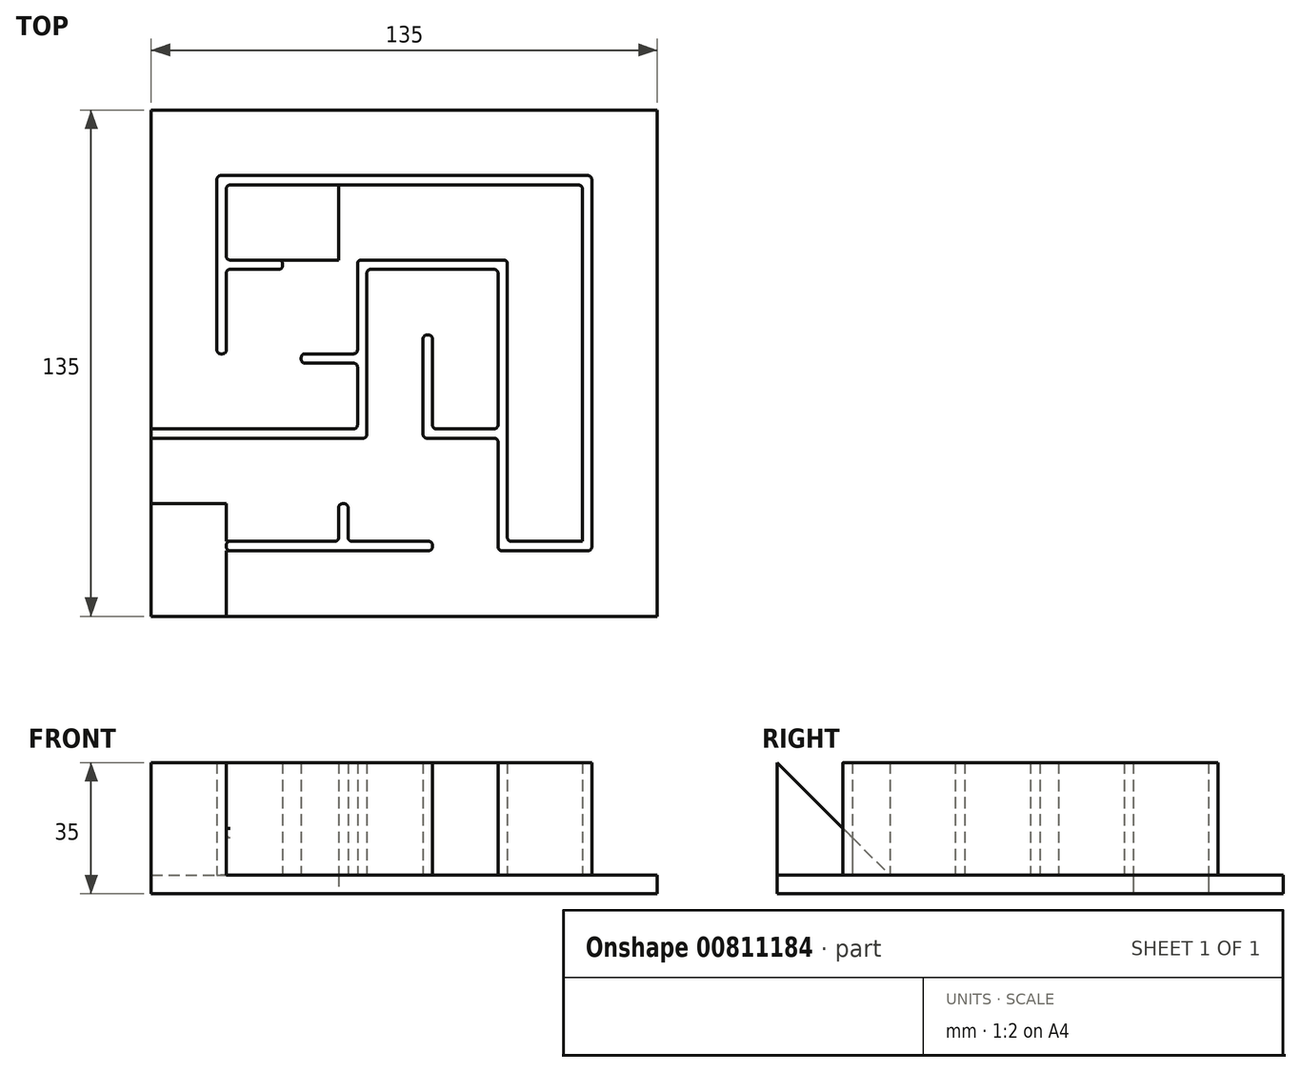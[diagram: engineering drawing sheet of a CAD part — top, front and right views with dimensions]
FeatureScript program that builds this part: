
annotation { "Feature Type Name" : "Feature", "Feature Type Description" : "" }
export const myFeature = defineFeature(function(context is Context, id is Id, definition is map)
    precondition{}
    {
        {
            var Q0;
            Q0=qCreatedBy(makeId("Top.planeOp"),FACE);
            var sketch = newSketch(context, id + "F0", { "sketchPlane" : qUnion([Q0])});
            skLineSegment(sketch, "E0.bottom", {"start": v(-67.5, 67.5) * mm, "end": v(67.5, 67.5) * mm});
            skLineSegment(sketch, "E0.top", {"start": v(-67.5, -67.5) * mm, "end": v(67.5, -67.5) * mm});
            skLineSegment(sketch, "E0.left", {"start": v(-67.5, 67.5) * mm, "end": v(-67.5, -67.5) * mm});
            skLineSegment(sketch, "E0.right", {"start": v(67.5, 67.5) * mm, "end": v(67.5, -67.5) * mm});
            skPoint(sketch, "E0.middle", {"position": v(0, 0) * mm});
            skLineSegment(sketch, "E1.bottom", {"start": v(-67.5, -67.5) * mm, "end": v(-47.5, -67.5) * mm});
            skLineSegment(sketch, "E1.top", {"start": v(-67.5, -37.5) * mm, "end": v(-47.5, -37.5) * mm});
            skLineSegment(sketch, "E1.left", {"start": v(-67.5, -67.5) * mm, "end": v(-67.5, -37.5) * mm});
            skLineSegment(sketch, "E1.right", {"start": v(-47.5, -67.5) * mm, "end": v(-47.5, -37.5) * mm});
            skLineSegment(sketch, "E2", {"start": v(-67.5, -17.5) * mm, "end": v(-12.5, -17.5) * mm});
            skLineSegment(sketch, "E3", {"start": v(-12.5, -17.5) * mm, "end": v(-12.5, 27.5) * mm});
            skLineSegment(sketch, "E4", {"start": v(-12.5, 27.5) * mm, "end": v(27.5, 27.5) * mm});
            skLineSegment(sketch, "E5", {"start": v(27.5, 27.5) * mm, "end": v(27.5, -47.5) * mm});
            skLineSegment(sketch, "E6", {"start": v(27.5, -47.5) * mm, "end": v(47.5, -47.5) * mm});
            skLineSegment(sketch, "E7", {"start": v(47.5, -47.5) * mm, "end": v(47.5, 47.5) * mm});
            skLineSegment(sketch, "E8", {"start": v(47.5, 47.5) * mm, "end": v(-47.5, 47.5) * mm});
            skLineSegment(sketch, "E9", {"start": v(-47.5, 47.5) * mm, "end": v(-47.5, 2.5) * mm});
            skLineSegment(sketch, "E10", {"start": v(27.5, -17.5) * mm, "end": v(7.5, -17.5) * mm});
            skLineSegment(sketch, "E11", {"start": v(7.5, -17.5) * mm, "end": v(7.5, 7.5) * mm});
            skLineSegment(sketch, "E12", {"start": v(-47.5, -47.5) * mm, "end": v(7.5, -47.5) * mm});
            skLineSegment(sketch, "E13", {"start": v(-12.5, 2.5) * mm, "end": v(-27.5, 2.5) * mm});
            skLineSegment(sketch, "E14", {"start": v(-47.5, 27.5) * mm, "end": v(-32.5, 27.5) * mm});
            skLineSegment(sketch, "E15", {"start": v(-17.5, -47.5) * mm, "end": v(-17.5, -37.5) * mm});
            skLineSegment(sketch, "E16.0", {"start": v(-10, -20) * mm, "end": v(-10, 27.5) * mm});
            skLineSegment(sketch, "E16.1", {"start": v(-67.5, -20) * mm, "end": v(-10, -20) * mm});
            skLineSegment(sketch, "E17.0", {"start": v(-47.5, -50) * mm, "end": v(7.5, -50) * mm});
            skLineSegment(sketch, "E18.0", {"start": v(-50, 50) * mm, "end": v(-50, 2.5) * mm});
            skLineSegment(sketch, "E18.1", {"start": v(50, 50) * mm, "end": v(-50, 50) * mm});
            skLineSegment(sketch, "E18.2", {"start": v(-12.5, 25) * mm, "end": v(25, 25) * mm});
            skLineSegment(sketch, "E18.3", {"start": v(25, 25) * mm, "end": v(25, -50) * mm});
            skLineSegment(sketch, "E18.4", {"start": v(25, -50) * mm, "end": v(50, -50) * mm});
            skLineSegment(sketch, "E18.5", {"start": v(50, -50) * mm, "end": v(50, 50) * mm});
            skLineSegment(sketch, "E19.0", {"start": v(-47.5, 25) * mm, "end": v(-32.5, 25) * mm});
            skLineSegment(sketch, "E20.0", {"start": v(-12.5, 0) * mm, "end": v(-27.5, 0) * mm});
            skLineSegment(sketch, "E21.0", {"start": v(5, -20) * mm, "end": v(5, 7.5) * mm});
            skLineSegment(sketch, "E21.1", {"start": v(27.5, -20) * mm, "end": v(5, -20) * mm});
            skLineSegment(sketch, "E22", {"start": v(7.5, -47.5) * mm, "end": v(7.5, -50) * mm});
            skLineSegment(sketch, "E23", {"start": v(-50, 2.5) * mm, "end": v(-47.5, 2.5) * mm});
            skLineSegment(sketch, "E24", {"start": v(5, 7.5) * mm, "end": v(7.5, 7.5) * mm});
            skLineSegment(sketch, "E25", {"start": v(-27.5, 0) * mm, "end": v(-27.5, 2.5) * mm});
            skLineSegment(sketch, "E26", {"start": v(-32.5, 25) * mm, "end": v(-32.5, 27.5) * mm});
            skLineSegment(sketch, "E27", {"start": v(-17.5, -37.5) * mm, "end": v(-15, -37.5) * mm});
            skLineSegment(sketch, "E28", {"start": v(-15, -37.5) * mm, "end": v(-15, -47.5) * mm});
            skLineSegment(sketch, "E29.bottom", {"start": v(-47.5, 27.5) * mm, "end": v(-17.5, 27.5) * mm});
            skLineSegment(sketch, "E29.top", {"start": v(-47.5, 47.5) * mm, "end": v(-17.5, 47.5) * mm});
            skLineSegment(sketch, "E29.left", {"start": v(-47.5, 27.5) * mm, "end": v(-47.5, 47.5) * mm});
            skLineSegment(sketch, "E29.right", {"start": v(-17.5, 27.5) * mm, "end": v(-17.5, 47.5) * mm});
            skSolve(sketch);
        }
        {
            var Q0;
            {var subQ29=sQuery(id+"F0.wireOp",EDGE,"E0.bottom");Q0=makeQuery(id+"F0.imprint","IMPRINT",FACE,{"disambiguationData":[TD([[makeQuery(id+"F0.imprint","IMPRINT",EDGE,{"derivedFrom":subQ29}),-1.0]])]});}
            extrude(context, id + "F1", {"entities" : qUnion([Q0]), "depth" : 5 * mm, "offsetDistance" : 25 * mm});
        }
        {
            var Q0;
            {var subQ0=sQuery(id+"F0.wireOp",EDGE,"E1.top");Q0=makeQuery(id+"F0.imprint","IMPRINT",FACE,{"disambiguationData":[TD([[makeQuery(id+"F0.imprint","IMPRINT",EDGE,{"derivedFrom":subQ0}),-1.0]])]});}
            extrude(context, id + "F2", {"entities" : qUnion([Q0]), "operationType" : NewBodyOperationType.ADD, "depth" : 35 * mm, "offsetDistance" : 25 * mm});
        }
        {
            var Q0;
            Q0=makeQuery(id+"F2.opExtrude","SWEPT_FACE",FACE,{"disambiguationData":[OSD([sQuery(id+"F0.wireOp",EDGE,"E1.right")])]});
            var sketch = newSketch(context, id + "F3", { "sketchPlane" : qUnion([Q0])});
            skLineSegment(sketch, "E30", {"start": v(-67.5, 35) * mm, "end": v(-37.5, 5) * mm});
            skSolve(sketch);
        }
        {
            var Q0;
            Q0=makeQuery(id+"F3.imprint","IMPRINT",FACE,{"disambiguationData":[TD([[makeQuery(id+"F3.imprint","IMPRINT",EDGE,{"derivedFrom":sQuery(id+"F3.wireOp",EDGE,"E30")}),1.0]])]});
            extrude(context, id + "F4", {"entities" : qUnion([Q0]), "operationType" : NewBodyOperationType.REMOVE, "oppositeDirection" : true, "depth" : 25 * mm, "offsetDistance" : 25 * mm});
        }
        {
            var Q0;
            {var subQ3=sQuery(id+"F0.wireOp",EDGE,"E6");Q0=makeQuery(id+"F0.imprint","IMPRINT",FACE,{"disambiguationData":[TD([[makeQuery(id+"F0.imprint","IMPRINT",EDGE,{"derivedFrom":subQ3}),-1.0]])]});}
            var Q1;
            {var subQ6=sQuery(id+"F0.wireOp",EDGE,"E17.0");Q1=makeQuery(id+"F0.imprint","IMPRINT",FACE,{"disambiguationData":[TD([[makeQuery(id+"F0.imprint","IMPRINT",EDGE,{"derivedFrom":subQ6}),1.0]])]});}
            var Q2;
            {var subQ1=sQuery(id+"F0.wireOp",EDGE,"E2");Q2=makeQuery(id+"F0.imprint","IMPRINT",FACE,{"disambiguationData":[TD([[makeQuery(id+"F0.imprint","IMPRINT",EDGE,{"derivedFrom":subQ1}),-1.0]])]});}
            var Q3;
            {var subQ0=sQuery(id+"F0.wireOp",EDGE,"E13");Q3=makeQuery(id+"F0.imprint","IMPRINT",FACE,{"disambiguationData":[TD([[makeQuery(id+"F0.imprint","IMPRINT",EDGE,{"derivedFrom":subQ0}),1.0]])]});}
            var Q4;
            {var subQ0=sQuery(id+"F0.wireOp",EDGE,"E14");Q4=makeQuery(id+"F0.imprint","IMPRINT",FACE,{"disambiguationData":[TD([[makeQuery(id+"F0.imprint","IMPRINT",EDGE,{"derivedFrom":subQ0}),-1.0]])]});}
            var Q5;
            {var subQ5=sQuery(id+"F0.wireOp",EDGE,"E4");var subQ7=sQuery(id+"F0.wireOp",EDGE,"E16.0");var subQ8=makeQuery(id+"F0.imprint","INTERSECT",VERTEX,{"derivedFrom":[subQ5,subQ7]});Q5=makeQuery(id+"F0.imprint","IMPRINT",FACE,{"disambiguationData":[TD([[makeQuery(id+"F0.imprint","IMPRINT",EDGE,{"disambiguationData":[TD([[subQ8,-1.0]])],"derivedFrom":subQ5}),-1.0]])]});}
            var Q6;
            {var subQ0=sQuery(id+"F0.wireOp",EDGE,"E4");var subQ1=sQuery(id+"F0.wireOp",EDGE,"E3");var subQ2=makeQuery(id+"F0.imprint","INTERSECT",VERTEX,{"derivedFrom":[subQ1,subQ0]});Q6=makeQuery(id+"F0.imprint","IMPRINT",FACE,{"disambiguationData":[TD([[makeQuery(id+"F0.imprint","IMPRINT",EDGE,{"disambiguationData":[TD([[subQ2,1.0]])],"derivedFrom":subQ1}),-1.0]])]});}
            var Q7;
            {var subQ1=sQuery(id+"F0.wireOp",EDGE,"E11");Q7=makeQuery(id+"F0.imprint","IMPRINT",FACE,{"disambiguationData":[TD([[makeQuery(id+"F0.imprint","IMPRINT",EDGE,{"derivedFrom":subQ1}),1.0]])]});}
            var Q8;
            {var subQ0=sQuery(id+"F0.wireOp",EDGE,"E21.1");var subQ1=sQuery(id+"F0.wireOp",EDGE,"E5");var subQ2=makeQuery(id+"F0.imprint","INTERSECT",VERTEX,{"derivedFrom":[subQ1,subQ0]});Q8=makeQuery(id+"F0.imprint","IMPRINT",FACE,{"disambiguationData":[TD([[makeQuery(id+"F0.imprint","IMPRINT",EDGE,{"disambiguationData":[TD([[subQ2,1.0]])],"derivedFrom":subQ1}),-1.0]])]});}
            var Q9;
            {var subQ2=sQuery(id+"F0.wireOp",EDGE,"E15");Q9=makeQuery(id+"F0.imprint","IMPRINT",FACE,{"disambiguationData":[TD([[makeQuery(id+"F0.imprint","IMPRINT",EDGE,{"derivedFrom":subQ2}),-1.0]])]});}
            var Q10;
            {var subQ2=sQuery(id+"F0.wireOp",EDGE,"E14");Q10=makeQuery(id+"F0.imprint","IMPRINT",FACE,{"disambiguationData":[TD([[makeQuery(id+"F0.imprint","IMPRINT",EDGE,{"derivedFrom":subQ2}),-1.0]])]});}
            extrude(context, id + "F5", {"entities" : qUnion([Q0, Q1, Q2, Q3, Q4, Q5, Q6, Q7, Q8, Q9, Q10]), "operationType" : NewBodyOperationType.ADD, "depth" : 35 * mm, "offsetDistance" : 25 * mm});
        }
        {
            var Q0;
            Q0=makeQuery(id+"F5.opExtrude","SWEPT_EDGE",EDGE,{"disambiguationData":[OSD([sQuery(id+"F0.wireOp",EDGE,"E17.0"),sQuery(id+"F0.wireOp",EDGE,"E22")])]});
            var Q1;
            Q1=makeQuery(id+"F5.opExtrude","SWEPT_EDGE",EDGE,{"disambiguationData":[OSD([sQuery(id+"F0.wireOp",EDGE,"E12"),sQuery(id+"F0.wireOp",EDGE,"E22")])]});
            var Q2;
            Q2=makeQuery(id+"F5.opExtrude","SWEPT_EDGE",EDGE,{"disambiguationData":[OSD([sQuery(id+"F0.wireOp",EDGE,"E16.0"),sQuery(id+"F0.wireOp",EDGE,"E16.1")])]});
            var Q3;
            Q3=makeQuery(id+"F5.opExtrude","SWEPT_EDGE",EDGE,{"disambiguationData":[OSD([sQuery(id+"F0.wireOp",EDGE,"E27"),sQuery(id+"F0.wireOp",EDGE,"E28")])]});
            var Q4;
            Q4=makeQuery(id+"F5.opExtrude","SWEPT_EDGE",EDGE,{"disambiguationData":[OSD([sQuery(id+"F0.wireOp",EDGE,"E21.0"),sQuery(id+"F0.wireOp",EDGE,"E21.1")])]});
            var Q5;
            Q5=makeQuery(id+"F5.opExtrude","SWEPT_EDGE",EDGE,{"disambiguationData":[OSD([sQuery(id+"F0.wireOp",EDGE,"E18.3"),sQuery(id+"F0.wireOp",EDGE,"E18.4")])]});
            var Q6;
            Q6=makeQuery(id+"F5.opExtrude","SWEPT_EDGE",EDGE,{"disambiguationData":[OSD([sQuery(id+"F0.wireOp",EDGE,"E18.4"),sQuery(id+"F0.wireOp",EDGE,"E18.5")])]});
            var Q7;
            Q7=makeQuery(id+"F5.opExtrude","SWEPT_EDGE",EDGE,{"disambiguationData":[OSD([sQuery(id+"F0.wireOp",EDGE,"E4"),sQuery(id+"F0.wireOp",EDGE,"E5")])]});
            var Q8;
            Q8=makeQuery(id+"F5.opExtrude","SWEPT_EDGE",EDGE,{"disambiguationData":[OSD([sQuery(id+"F0.wireOp",EDGE,"E18.1"),sQuery(id+"F0.wireOp",EDGE,"E18.5")])]});
            var Q9;
            Q9=makeQuery(id+"F5.opExtrude","SWEPT_EDGE",EDGE,{"disambiguationData":[OSD([sQuery(id+"F0.wireOp",EDGE,"E8"),sQuery(id+"F0.wireOp",EDGE,"E9")])]});
            var Q10;
            Q10=makeQuery(id+"F5.opExtrude","SWEPT_EDGE",EDGE,{"disambiguationData":[OSD([sQuery(id+"F0.wireOp",EDGE,"E20.0"),sQuery(id+"F0.wireOp",EDGE,"E25")])]});
            var Q11;
            {var subQ0=sQuery(id+"F0.wireOp",EDGE,"E1.right");var subQ1=sQuery(id+"F0.wireOp",EDGE,"E17.0");Q11=makeQuery(id+"F5.boolean.opBoolean","SPLIT",EDGE,{"disambiguationData":[topologyDisambiguationEdgeConnected([makeQuery(id+"F5.opExtrude","SWEPT_FACE",FACE,{"disambiguationData":[OSD([subQ0])]})])],"derivedFrom":makeQuery(id+"F5.opExtrude","SWEPT_EDGE",EDGE,{"disambiguationData":[OSD([subQ0,subQ1])]})});}
            var Q12;
            Q12=makeQuery(id+"F5.opExtrude","SWEPT_EDGE",EDGE,{"disambiguationData":[OSD([sQuery(id+"F0.wireOp",EDGE,"E9"),sQuery(id+"F0.wireOp",EDGE,"E19.0")])]});
            var Q13;
            Q13=makeQuery(id+"F5.opExtrude","SWEPT_EDGE",EDGE,{"disambiguationData":[OSD([sQuery(id+"F0.wireOp",EDGE,"E19.0"),sQuery(id+"F0.wireOp",EDGE,"E26")])]});
            var Q14;
            Q14=makeQuery(id+"F5.opExtrude","SWEPT_EDGE",EDGE,{"disambiguationData":[OSD([sQuery(id+"F0.wireOp",EDGE,"E14"),sQuery(id+"F0.wireOp",EDGE,"E26"),sQuery(id+"F0.wireOp",EDGE,"E29.bottom")])]});
            var Q15;
            Q15=makeQuery(id+"F5.opExtrude","SWEPT_EDGE",EDGE,{"disambiguationData":[OSD([sQuery(id+"F0.wireOp",EDGE,"E16.0"),sQuery(id+"F0.wireOp",EDGE,"E18.2")])]});
            var Q16;
            Q16=makeQuery(id+"F5.opExtrude","SWEPT_EDGE",EDGE,{"disambiguationData":[OSD([sQuery(id+"F0.wireOp",EDGE,"E11"),sQuery(id+"F0.wireOp",EDGE,"E24")])]});
            var Q17;
            Q17=makeQuery(id+"F5.opExtrude","SWEPT_EDGE",EDGE,{"disambiguationData":[OSD([sQuery(id+"F0.wireOp",EDGE,"E9"),sQuery(id+"F0.wireOp",EDGE,"E23")])]});
            var Q18;
            Q18=makeQuery(id+"F5.opExtrude","SWEPT_EDGE",EDGE,{"disambiguationData":[OSD([sQuery(id+"F0.wireOp",EDGE,"E18.0"),sQuery(id+"F0.wireOp",EDGE,"E23")])]});
            var Q19;
            {var subQ0=sQuery(id+"F0.wireOp",EDGE,"E1.right");var subQ1=sQuery(id+"F0.wireOp",EDGE,"E12");Q19=makeQuery(id+"F5.boolean.opBoolean","SPLIT",EDGE,{"disambiguationData":[topologyDisambiguationEdgeConnected([makeQuery(id+"F5.opExtrude","SWEPT_FACE",FACE,{"disambiguationData":[OSD([subQ0])]})])],"derivedFrom":makeQuery(id+"F5.opExtrude","SWEPT_EDGE",EDGE,{"disambiguationData":[OSD([subQ0,subQ1])]})});}
            var Q20;
            Q20=makeQuery(id+"F5.opExtrude","SWEPT_EDGE",EDGE,{"disambiguationData":[OSD([sQuery(id+"F0.wireOp",EDGE,"E18.0"),sQuery(id+"F0.wireOp",EDGE,"E18.1")])]});
            var Q21;
            Q21=makeQuery(id+"F5.opExtrude","SWEPT_EDGE",EDGE,{"disambiguationData":[OSD([sQuery(id+"F0.wireOp",EDGE,"E18.3"),sQuery(id+"F0.wireOp",EDGE,"E21.1")])]});
            var Q22;
            Q22=makeQuery(id+"F5.opExtrude","SWEPT_EDGE",EDGE,{"disambiguationData":[OSD([sQuery(id+"F0.wireOp",EDGE,"E3"),sQuery(id+"F0.wireOp",EDGE,"E13")])]});
            var Q23;
            Q23=makeQuery(id+"F5.opExtrude","SWEPT_EDGE",EDGE,{"disambiguationData":[OSD([sQuery(id+"F0.wireOp",EDGE,"E10"),sQuery(id+"F0.wireOp",EDGE,"E18.3")])]});
            var Q24;
            Q24=makeQuery(id+"F5.opExtrude","SWEPT_EDGE",EDGE,{"disambiguationData":[OSD([sQuery(id+"F0.wireOp",EDGE,"E2"),sQuery(id+"F0.wireOp",EDGE,"E3")])]});
            var Q25;
            Q25=makeQuery(id+"F5.opExtrude","SWEPT_EDGE",EDGE,{"disambiguationData":[OSD([sQuery(id+"F0.wireOp",EDGE,"E5"),sQuery(id+"F0.wireOp",EDGE,"E6")])]});
            var Q26;
            Q26=makeQuery(id+"F5.opExtrude","SWEPT_EDGE",EDGE,{"disambiguationData":[OSD([sQuery(id+"F0.wireOp",EDGE,"E3"),sQuery(id+"F0.wireOp",EDGE,"E4")])]});
            var Q27;
            {var subQ0=sQuery(id+"F3.wireOp",EDGE,"E30");var subQ1=makeQuery(id+"F4.boolean.opBoolean","COPY",FACE,{"derivedFrom":makeQuery(id+"F4.opExtrude","SWEPT_FACE",FACE,{"disambiguationData":[OSD([subQ0])]})});var subQ2=sQuery(id+"F0.wireOp",EDGE,"E12");var subQ3=sQuery(id+"F0.wireOp",EDGE,"E1.right");var subQ5=makeQuery(id+"F2.opExtrude","SWEPT_FACE",FACE,{"disambiguationData":[OSD([subQ3])]});Q27=makeQuery(id+"F5.boolean.opBoolean","SPLIT",EDGE,{"disambiguationData":[topologyDisambiguationEdgeConnected([subQ5,subQ1]),TD([makeQuery(id+"F5.opExtrude","SWEPT_FACE",FACE,{"disambiguationData":[OSD([subQ2]),TDD([makeQuery(id+"F0.imprint","IMPRINT",EDGE,{"disambiguationData":[TD([[makeQuery(id+"F0.imprint","INTERSECT",VERTEX,{"derivedFrom":[subQ3,subQ2]}),-1.0]])],"derivedFrom":subQ2})])]})])],"derivedFrom":makeQuery(id+"F4.boolean.opBoolean","COPY",EDGE,{"derivedFrom":makeQuery(id+"F4.opExtrude","CAP_EDGE",EDGE,{"disambiguationData":[OSD([subQ0])],"isStart":true})})});}
            var Q28;
            Q28=makeQuery(id+"F5.opExtrude","SWEPT_EDGE",EDGE,{"disambiguationData":[OSD([sQuery(id+"F0.wireOp",EDGE,"E9"),sQuery(id+"F0.wireOp",EDGE,"E14")])]});
            var Q29;
            Q29=makeQuery(id+"F5.opExtrude","SWEPT_EDGE",EDGE,{"disambiguationData":[OSD([sQuery(id+"F0.wireOp",EDGE,"E10"),sQuery(id+"F0.wireOp",EDGE,"E11")])]});
            var Q30;
            Q30=makeQuery(id+"F5.opExtrude","SWEPT_EDGE",EDGE,{"disambiguationData":[OSD([sQuery(id+"F0.wireOp",EDGE,"E15"),sQuery(id+"F0.wireOp",EDGE,"E27")])]});
            var Q31;
            Q31=makeQuery(id+"F5.opExtrude","SWEPT_EDGE",EDGE,{"disambiguationData":[OSD([sQuery(id+"F0.wireOp",EDGE,"E18.2"),sQuery(id+"F0.wireOp",EDGE,"E18.3")])]});
            fillet(context, id + "F6", {"entities" : qUnion([Q0, Q1, Q2, Q3, Q4, Q5, Q6, Q7, Q8, Q9, Q10, Q11, Q12, Q13, Q14, Q15, Q16, Q17, Q18, Q19, Q20, Q21, Q22, Q23, Q24, Q25, Q26, Q27, Q28, Q29, Q30, Q31]), "radius" : 1 * mm, "tangentPropagation" : true, "allowEdgeOverflow" : false});
        }
        {
            var Q0;
            Q0=makeQuery(id+"F5.opExtrude","SWEPT_EDGE",EDGE,{"disambiguationData":[OSD([sQuery(id+"F0.wireOp",EDGE,"E17.0"),sQuery(id+"F0.wireOp",EDGE,"E22")])]});
            var Q1;
            Q1=makeQuery(id+"F5.opExtrude","SWEPT_EDGE",EDGE,{"disambiguationData":[OSD([sQuery(id+"F0.wireOp",EDGE,"E12"),sQuery(id+"F0.wireOp",EDGE,"E22")])]});
            var Q2;
            Q2=makeQuery(id+"F5.opExtrude","SWEPT_EDGE",EDGE,{"disambiguationData":[OSD([sQuery(id+"F0.wireOp",EDGE,"E27"),sQuery(id+"F0.wireOp",EDGE,"E28")])]});
            var Q3;
            Q3=makeQuery(id+"F5.opExtrude","SWEPT_EDGE",EDGE,{"disambiguationData":[OSD([sQuery(id+"F0.wireOp",EDGE,"E21.0"),sQuery(id+"F0.wireOp",EDGE,"E21.1")])]});
            var Q4;
            Q4=makeQuery(id+"F5.opExtrude","SWEPT_EDGE",EDGE,{"disambiguationData":[OSD([sQuery(id+"F0.wireOp",EDGE,"E16.0"),sQuery(id+"F0.wireOp",EDGE,"E16.1")])]});
            var Q5;
            Q5=makeQuery(id+"F5.opExtrude","SWEPT_EDGE",EDGE,{"disambiguationData":[OSD([sQuery(id+"F0.wireOp",EDGE,"E18.3"),sQuery(id+"F0.wireOp",EDGE,"E18.4")])]});
            var Q6;
            Q6=makeQuery(id+"F5.opExtrude","SWEPT_EDGE",EDGE,{"disambiguationData":[OSD([sQuery(id+"F0.wireOp",EDGE,"E18.4"),sQuery(id+"F0.wireOp",EDGE,"E18.5")])]});
            var Q7;
            Q7=makeQuery(id+"F5.opExtrude","SWEPT_EDGE",EDGE,{"disambiguationData":[OSD([sQuery(id+"F0.wireOp",EDGE,"E18.1"),sQuery(id+"F0.wireOp",EDGE,"E18.5")])]});
            var Q8;
            Q8=makeQuery(id+"F5.opExtrude","SWEPT_EDGE",EDGE,{"disambiguationData":[OSD([sQuery(id+"F0.wireOp",EDGE,"E4"),sQuery(id+"F0.wireOp",EDGE,"E5")])]});
            var Q9;
            Q9=makeQuery(id+"F5.opExtrude","SWEPT_EDGE",EDGE,{"disambiguationData":[OSD([sQuery(id+"F0.wireOp",EDGE,"E16.0"),sQuery(id+"F0.wireOp",EDGE,"E18.2")])]});
            var Q10;
            Q10=makeQuery(id+"F5.opExtrude","SWEPT_EDGE",EDGE,{"disambiguationData":[OSD([sQuery(id+"F0.wireOp",EDGE,"E19.0"),sQuery(id+"F0.wireOp",EDGE,"E26")])]});
            var Q11;
            Q11=makeQuery(id+"F5.opExtrude","SWEPT_EDGE",EDGE,{"disambiguationData":[OSD([sQuery(id+"F0.wireOp",EDGE,"E14"),sQuery(id+"F0.wireOp",EDGE,"E26"),sQuery(id+"F0.wireOp",EDGE,"E29.bottom")])]});
            var Q12;
            Q12=makeQuery(id+"F5.opExtrude","SWEPT_EDGE",EDGE,{"disambiguationData":[OSD([sQuery(id+"F0.wireOp",EDGE,"E8"),sQuery(id+"F0.wireOp",EDGE,"E9")])]});
            var Q13;
            Q13=makeQuery(id+"F5.opExtrude","SWEPT_EDGE",EDGE,{"disambiguationData":[OSD([sQuery(id+"F0.wireOp",EDGE,"E9"),sQuery(id+"F0.wireOp",EDGE,"E19.0")])]});
            var Q14;
            Q14=makeQuery(id+"F5.opExtrude","SWEPT_EDGE",EDGE,{"disambiguationData":[OSD([sQuery(id+"F0.wireOp",EDGE,"E9"),sQuery(id+"F0.wireOp",EDGE,"E23")])]});
            var Q15;
            Q15=makeQuery(id+"F5.opExtrude","SWEPT_EDGE",EDGE,{"disambiguationData":[OSD([sQuery(id+"F0.wireOp",EDGE,"E18.0"),sQuery(id+"F0.wireOp",EDGE,"E23")])]});
            var Q16;
            Q16=makeQuery(id+"F5.opExtrude","SWEPT_EDGE",EDGE,{"disambiguationData":[OSD([sQuery(id+"F0.wireOp",EDGE,"E20.0"),sQuery(id+"F0.wireOp",EDGE,"E25")])]});
            var Q17;
            Q17=makeQuery(id+"F5.opExtrude","SWEPT_EDGE",EDGE,{"disambiguationData":[OSD([sQuery(id+"F0.wireOp",EDGE,"E11"),sQuery(id+"F0.wireOp",EDGE,"E24")])]});
            var Q18;
            {var subQ0=sQuery(id+"F0.wireOp",EDGE,"E1.right");var subQ1=sQuery(id+"F0.wireOp",EDGE,"E12");Q18=makeQuery(id+"F5.boolean.opBoolean","SPLIT",EDGE,{"disambiguationData":[topologyDisambiguationEdgeConnected([makeQuery(id+"F5.opExtrude","SWEPT_FACE",FACE,{"disambiguationData":[OSD([subQ0])]})])],"derivedFrom":makeQuery(id+"F5.opExtrude","SWEPT_EDGE",EDGE,{"disambiguationData":[OSD([subQ0,subQ1])]})});}
            var Q19;
            Q19=makeQuery(id+"F5.opExtrude","SWEPT_EDGE",EDGE,{"disambiguationData":[OSD([sQuery(id+"F0.wireOp",EDGE,"E13"),sQuery(id+"F0.wireOp",EDGE,"E25")])]});
            var Q20;
            Q20=makeQuery(id+"F5.opExtrude","SWEPT_EDGE",EDGE,{"disambiguationData":[OSD([sQuery(id+"F0.wireOp",EDGE,"E3"),sQuery(id+"F0.wireOp",EDGE,"E20.0")])]});
            var Q21;
            Q21=makeQuery(id+"F5.opExtrude","SWEPT_EDGE",EDGE,{"disambiguationData":[OSD([sQuery(id+"F0.wireOp",EDGE,"E18.2"),sQuery(id+"F0.wireOp",EDGE,"E18.3")])]});
            var Q22;
            Q22=makeQuery(id+"F5.opExtrude","SWEPT_EDGE",EDGE,{"disambiguationData":[OSD([sQuery(id+"F0.wireOp",EDGE,"E18.3"),sQuery(id+"F0.wireOp",EDGE,"E21.1")])]});
            var Q23;
            Q23=makeQuery(id+"F5.opExtrude","SWEPT_EDGE",EDGE,{"disambiguationData":[OSD([sQuery(id+"F0.wireOp",EDGE,"E3"),sQuery(id+"F0.wireOp",EDGE,"E4")])]});
            var Q24;
            Q24=makeQuery(id+"F5.opExtrude","SWEPT_EDGE",EDGE,{"disambiguationData":[OSD([sQuery(id+"F0.wireOp",EDGE,"E18.0"),sQuery(id+"F0.wireOp",EDGE,"E18.1")])]});
            var Q25;
            Q25=makeQuery(id+"F5.opExtrude","SWEPT_EDGE",EDGE,{"disambiguationData":[OSD([sQuery(id+"F0.wireOp",EDGE,"E7"),sQuery(id+"F0.wireOp",EDGE,"E8")])]});
            var Q26;
            Q26=makeQuery(id+"F5.opExtrude","SWEPT_EDGE",EDGE,{"disambiguationData":[OSD([sQuery(id+"F0.wireOp",EDGE,"E3"),sQuery(id+"F0.wireOp",EDGE,"E13")])]});
            var Q27;
            Q27=makeQuery(id+"F5.opExtrude","SWEPT_EDGE",EDGE,{"disambiguationData":[OSD([sQuery(id+"F0.wireOp",EDGE,"E2"),sQuery(id+"F0.wireOp",EDGE,"E3")])]});
            var Q28;
            Q28=makeQuery(id+"F5.opExtrude","SWEPT_EDGE",EDGE,{"disambiguationData":[OSD([sQuery(id+"F0.wireOp",EDGE,"E12"),sQuery(id+"F0.wireOp",EDGE,"E15")])]});
            var Q29;
            Q29=makeQuery(id+"F5.opExtrude","SWEPT_EDGE",EDGE,{"disambiguationData":[OSD([sQuery(id+"F0.wireOp",EDGE,"E15"),sQuery(id+"F0.wireOp",EDGE,"E27")])]});
            var Q30;
            Q30=makeQuery(id+"F5.opExtrude","SWEPT_EDGE",EDGE,{"disambiguationData":[OSD([sQuery(id+"F0.wireOp",EDGE,"E10"),sQuery(id+"F0.wireOp",EDGE,"E18.3")])]});
            var Q31;
            Q31=makeQuery(id+"F5.opExtrude","SWEPT_EDGE",EDGE,{"disambiguationData":[OSD([sQuery(id+"F0.wireOp",EDGE,"E21.0"),sQuery(id+"F0.wireOp",EDGE,"E24")])]});
            var Q32;
            Q32=makeQuery(id+"F5.opExtrude","SWEPT_EDGE",EDGE,{"disambiguationData":[OSD([sQuery(id+"F0.wireOp",EDGE,"E5"),sQuery(id+"F0.wireOp",EDGE,"E6")])]});
            var Q33;
            Q33=makeQuery(id+"F5.opExtrude","SWEPT_EDGE",EDGE,{"disambiguationData":[OSD([sQuery(id+"F0.wireOp",EDGE,"E12"),sQuery(id+"F0.wireOp",EDGE,"E28")])]});
            var Q34;
            Q34=makeQuery(id+"F5.opExtrude","SWEPT_EDGE",EDGE,{"disambiguationData":[OSD([sQuery(id+"F0.wireOp",EDGE,"E10"),sQuery(id+"F0.wireOp",EDGE,"E11")])]});
            var Q35;
            Q35=makeQuery(id+"F5.opExtrude","SWEPT_EDGE",EDGE,{"disambiguationData":[OSD([sQuery(id+"F0.wireOp",EDGE,"E9"),sQuery(id+"F0.wireOp",EDGE,"E14")])]});
            fillet(context, id + "F7", {"entities" : qUnion([Q0, Q1, Q2, Q3, Q4, Q5, Q6, Q7, Q8, Q9, Q10, Q11, Q12, Q13, Q14, Q15, Q16, Q17, Q18, Q19, Q20, Q21, Q22, Q23, Q24, Q25, Q26, Q27, Q28, Q29, Q30, Q31, Q32, Q33, Q34, Q35]), "radius" : 1 * mm, "tangentPropagation" : true, "allowEdgeOverflow" : false});
        }
    });
